# Revit family: PRD_AR_MxrTps_ThermostaticWall-mountedMixer_F4ET1001
name_source: partatom
category: Plumbing Fixtures
units: mm (PartAtom-declared; Revit-internal decimal feet)

## family parameters
Cut with Voids When Loaded = Yes
Host = Face
OmniClass Number = 23.45.55.17
OmniClass Title = Mixing Faucets
Part Type = Normal
Room Calculation Point = No
Round Connector Dimension = Use Diameter
Shared = No

## types (1)
- F4ET1001
    AccentColour = none
    AdjustableFlowTime = yes
    AssetType = Fixed
    BIMObjectName = PRD_AR_MixerTaps_ThermostaticWall-mountedMixer_F4ET1001
    BasicColour = chrome-look (glossy)
    BodyMaterial = PRD_AR_ChromatedBrass_HighPolished
    Category = Pr_40_20_87_55, Mixer taps
    CloseOffRating = 0.0 Pa
    Color = chrome-look (glossy)
    CompatibleA3000Open = no
    Default Elevation = 1219 mm
    DefaultAutomaticHygieneFlush = 24h after the last activity
    Depressurised = no
    Description = F4ET-Med thermostatic wall-mounted mixer as DN 15 wall-mounted mixer, for wall mounting with lockable swivelling spout, for sanitary facilities in the healthcare and nursing sector. Opto-electronically controlled, triggered by hand movement with subsequent automatic switching to body detection. Thermostat with metal handle, including lever for reduced-touch operation, and adjustable, turn-proof temperature stop. With the option of manual thermal disinfection. For connecting to hot and cold water. Control electronics, stagnation-free hygiene solenoid valve cartridge, flowrate controller 9.0 l/min, 6 V lithium battery (CR-P2) and sensor in the scald-protected safe-touch housing, polished chromium-plated brass. Decoupled from the tap housing, volume-reduced, smooth water flow from low-lead brass (lead proportion ≤ 0.2%), and without nickel coating. With thermal insulation components to reduce heat transfer from the tap housing to the cold-water line. Self-emptying spout with laminar jet controller. With adjustable and lockable connections with backflow preventers and strainers, fully covered by depth-adjustable screw rosettes. 210 mm projection. Activated water hygiene flushing 24 hours after last activation, safety switch-off for continuous reflection and saving of statistical data. With option for parametrisation and communication via optional, bidirectional remote control.
    DiameterNominal = 15  [stored 0.0492126 ft]
    DurationUnit = year
    FaucetFunction = Mixed
    FaucetOperation = ELECTRONIC
    FaucetType = Bib
    Features = For connection to hot water and cold water. Flowrate controller 9.0 l/min. 210 mm projection.
    Finish = polished chrome-plated
    FlowCoefficient = 0
    FunctionalPrinciple = electronic self-closing
    HygieneFlushing = yes
    IfcExportAs = IfcValveType
    IfcExportType = FAUCET
    InletSize = G 1/2 B
    LockingMechanism = Top section, non-ceramic
    Manufacturer = KWC Group AG
    ManufacturerName = KWC Group AG
    ManufacturerURL = www.kwc.com
    Material = Brass
    MaterialFitting = brass-look
    Maximum FlowTime = 255 Seconds
    MinimumFlowPressure = 1 bar
    MinimumFlowTime = 1 Seconds
    Model = F4ET1001
    ModelNumber = 2030072424
    ModelReference = F4ET1001
    NBSDescription = Taps and water supply fittings for sinks
    NBSReference = 45-35-70/345
    Name = F4ET-Med thermostatic wall-mounted mixer F4ET1001
    NominalDepth = 0 mm  [stored 0 ft]
    NominalHeight = 0 mm  [stored 0 ft]
    NominalWidth = 316 mm
    NumberOfBatteries = 1
    OverallWidth = 316 mm
    Parametrization = remote control
    Pop-upWasteSet = no
    PowerSupplyConnection = Battery 6 V
    ProductInformation = http://pim.kwc.com
    ProtectiveShutdown = yes
    ProtectiveSystemIP = IP59K
    Shape = Bib tap
    Size = 15
    Spout = rotating, bottom
    SpoutProjection = 115 mm
    Status = New
    SurfaceFinishFitting = chromed
    SurfaceTreatmentFitting = polished
    TailorMade = no
    TemperatureLimit = yes
    TestPressure = 0.0 Pa
    ThermalDisinfection = manual thermal disinfection
    TypeOfBatteries = CR-P2 Lithium battery 6V
    TypeOfMixing = with thermostat
    TypeOfMounting = wall mounting
    TypeOfOperation = sensor operation
    TypeOfPowerSupply = Battery
    TypeOfSensor = opto-electronic sensor
    TypeOfTap = bib tap
    URL = www.kwc.com
    Uniclass2015Code = Pr_40_20_87_55
    Uniclass2015Title = Mixer taps
    Uniclass2015Version = Products v1.32
    ValveMechanism = OTHER
    ValveOperation = OTHER
    ValvePattern = STRAIGHT_3_PORT
    Version = 1
    VolumeFlowRate = 0.15 l/s at 3 bar
    WarrantyDurationUnit = year
    WaterConnection = S-unions
    WithBackflowPreventer = yes
    WithFilter = yes
    WithRosettesOrCoverPlate = yes
    WithTransformerOrPowerSupply = no
    WorkingPressure = 0.0 Pa

note: [stored X ft] marks values corroborated as IEEE doubles in the binary element streams (Revit-internal decimal feet)

## geometry (parser evidence)
native form markers: Sweep x5
no freeform markers — native parametric forms only
